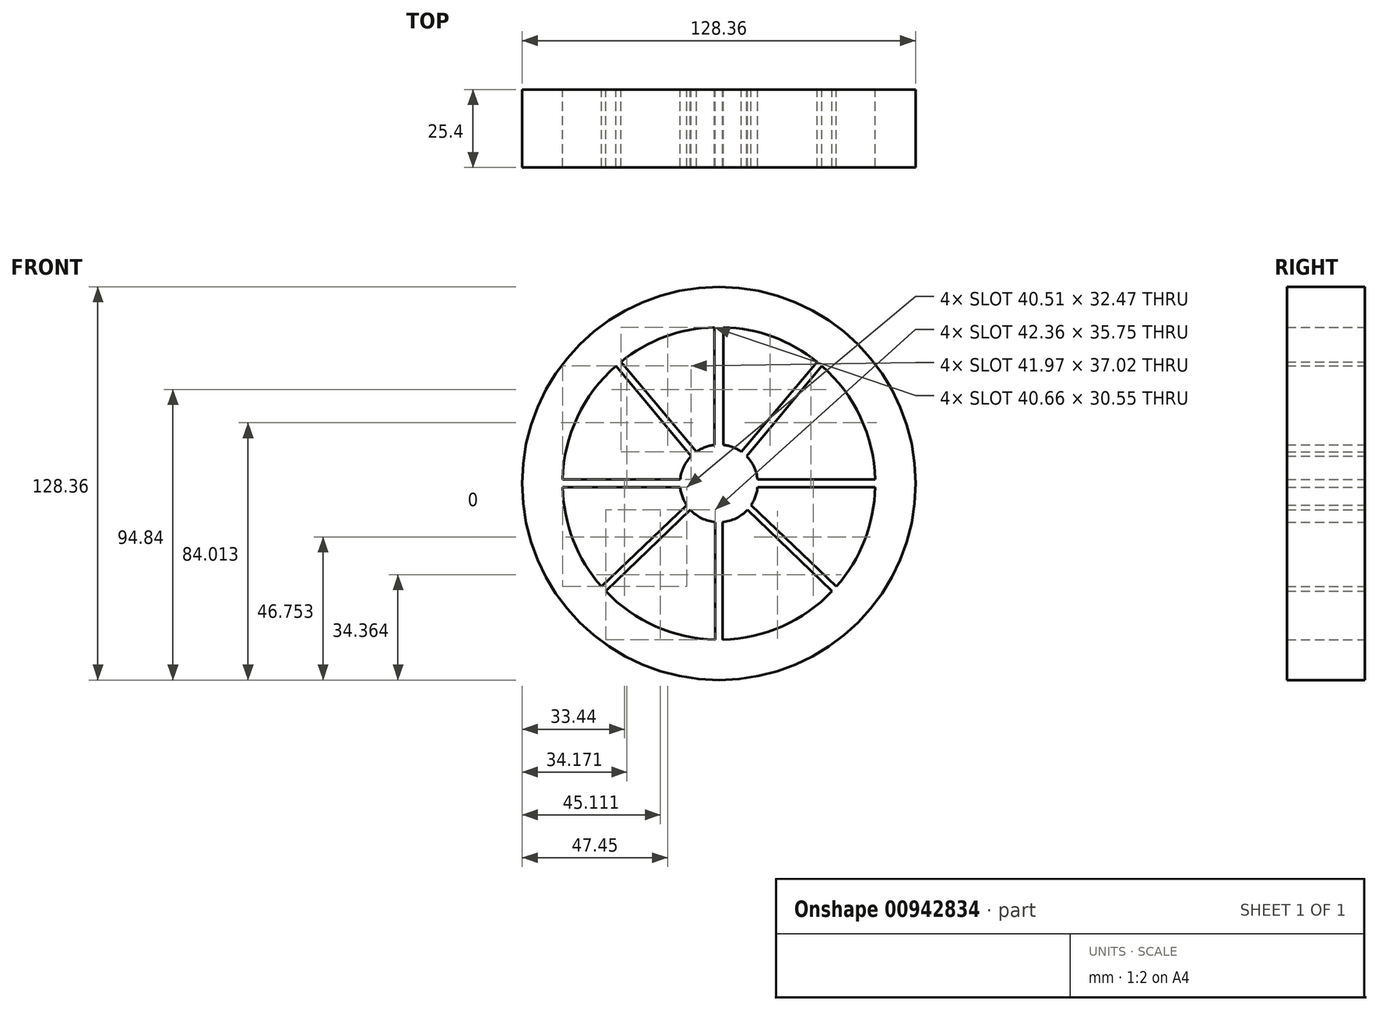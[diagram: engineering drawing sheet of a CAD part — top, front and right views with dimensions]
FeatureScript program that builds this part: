
annotation { "Feature Type Name" : "Feature", "Feature Type Description" : "" }
export const myFeature = defineFeature(function(context is Context, id is Id, definition is map)
    precondition{}
    {
        {
            var Q0;
            Q0=qCreatedBy(makeId("Front.planeOp"),FACE);
            var sketch = newSketch(context, id + "F0", { "sketchPlane" : qUnion([Q0])});
            skCircle(sketch, "E0", {"center": v(0, 0) * mm, "radius": 51 * mm});
            skCircle(sketch, "E1", {"center": v(0, 0) * mm, "radius": 12.67 * mm});
            skLineSegment(sketch, "E2", {"start": v(-1.46, 12.6) * mm, "end": v(-1.46, 50.99) * mm});
            skLineSegment(sketch, "E3", {"start": v(-7.34, 10.33) * mm, "end": v(-32, 39.72) * mm});
            skLineSegment(sketch, "E4", {"start": v(-9.03, 8.9) * mm, "end": v(-33.64, 38.34) * mm});
            skLineSegment(sketch, "E5", {"start": v(-12.6, 1.32) * mm, "end": v(-51, 1.32) * mm});
            skLineSegment(sketch, "E6", {"start": v(-12.62, -1.2) * mm, "end": v(-51, -1.2) * mm});
            skLineSegment(sketch, "E7", {"start": v(-10.49, -7.12) * mm, "end": v(-38.33, -33.66) * mm});
            skLineSegment(sketch, "E8", {"start": v(-9.28, -8.64) * mm, "end": v(-36.94, -35.17) * mm});
            skLineSegment(sketch, "E9", {"start": v(-1.2, -12.62) * mm, "end": v(-1.2, -51) * mm});
            skLineSegment(sketch, "E10.MirrorCS", {"start": v(7.34, 10.33) * mm, "end": v(32, 39.72) * mm});
            skLineSegment(sketch, "E11.MirrorCS", {"start": v(9.03, 8.9) * mm, "end": v(33.64, 38.34) * mm});
            skLineSegment(sketch, "E12.MirrorCS", {"start": v(12.6, 1.32) * mm, "end": v(51, 1.32) * mm});
            skLineSegment(sketch, "E13.MirrorCS", {"start": v(12.62, -1.2) * mm, "end": v(51, -1.2) * mm});
            skLineSegment(sketch, "E14.MirrorCS", {"start": v(10.49, -7.12) * mm, "end": v(38.33, -33.66) * mm});
            skLineSegment(sketch, "E15.MirrorCS", {"start": v(9.28, -8.64) * mm, "end": v(36.94, -35.17) * mm});
            skLineSegment(sketch, "E16.MirrorCS", {"start": v(1.46, 12.6) * mm, "end": v(1.46, 50.99) * mm});
            skLineSegment(sketch, "E17.MirrorCS", {"start": v(1.2, -12.62) * mm, "end": v(1.2, -51) * mm});
            skCircle(sketch, "E18", {"center": v(0, 0) * mm, "radius": 64.18 * mm});
            skSolve(sketch);
        }
        {
            var Q0;
            Q0=makeQuery(id+"F0.imprint","IMPRINT",FACE,{"disambiguationData":[TD([[makeQuery(id+"F0.imprint","IMPRINT",EDGE,{"derivedFrom":sQuery(id+"F0.wireOp",EDGE,"E18")}),1.0]])]});
            var Q1;
            {var subQ0=sQuery(id+"F0.wireOp",EDGE,"E3");Q1=makeQuery(id+"F0.imprint","IMPRINT",FACE,{"disambiguationData":[TD([[makeQuery(id+"F0.imprint","IMPRINT",EDGE,{"derivedFrom":subQ0}),1.0]])]});}
            var Q2;
            {var subQ0=sQuery(id+"F0.wireOp",EDGE,"E2");Q2=makeQuery(id+"F0.imprint","IMPRINT",FACE,{"disambiguationData":[TD([[makeQuery(id+"F0.imprint","IMPRINT",EDGE,{"derivedFrom":subQ0}),-1.0]])]});}
            var Q3;
            {var subQ0=sQuery(id+"F0.wireOp",EDGE,"E10.MirrorCS");Q3=makeQuery(id+"F0.imprint","IMPRINT",FACE,{"disambiguationData":[TD([[makeQuery(id+"F0.imprint","IMPRINT",EDGE,{"derivedFrom":subQ0}),-1.0]])]});}
            var Q4;
            {var subQ0=sQuery(id+"F0.wireOp",EDGE,"E1");var subQ8=makeQuery(id+"F0.imprint","INTERSECT",VERTEX,{"derivedFrom":[subQ0,sQuery(id+"F0.wireOp",EDGE,"E11.MirrorCS")]});Q4=makeQuery(id+"F0.imprint","IMPRINT",FACE,{"disambiguationData":[TD([[makeQuery(id+"F0.imprint","IMPRINT",EDGE,{"disambiguationData":[TD([[subQ8,1.0]])],"derivedFrom":subQ0}),1.0]])]});}
            var Q5;
            {var subQ0=sQuery(id+"F0.wireOp",EDGE,"E12.MirrorCS");Q5=makeQuery(id+"F0.imprint","IMPRINT",FACE,{"disambiguationData":[TD([[makeQuery(id+"F0.imprint","IMPRINT",EDGE,{"derivedFrom":subQ0}),-1.0]])]});}
            var Q6;
            {var subQ0=sQuery(id+"F0.wireOp",EDGE,"E14.MirrorCS");Q6=makeQuery(id+"F0.imprint","IMPRINT",FACE,{"disambiguationData":[TD([[makeQuery(id+"F0.imprint","IMPRINT",EDGE,{"derivedFrom":subQ0}),-1.0]])]});}
            var Q7;
            {var subQ0=sQuery(id+"F0.wireOp",EDGE,"E9");Q7=makeQuery(id+"F0.imprint","IMPRINT",FACE,{"disambiguationData":[TD([[makeQuery(id+"F0.imprint","IMPRINT",EDGE,{"derivedFrom":subQ0}),1.0]])]});}
            var Q8;
            {var subQ0=sQuery(id+"F0.wireOp",EDGE,"E7");Q8=makeQuery(id+"F0.imprint","IMPRINT",FACE,{"disambiguationData":[TD([[makeQuery(id+"F0.imprint","IMPRINT",EDGE,{"derivedFrom":subQ0}),1.0]])]});}
            var Q9;
            {var subQ0=sQuery(id+"F0.wireOp",EDGE,"E5");Q9=makeQuery(id+"F0.imprint","IMPRINT",FACE,{"disambiguationData":[TD([[makeQuery(id+"F0.imprint","IMPRINT",EDGE,{"derivedFrom":subQ0}),1.0]])]});}
            extrude(context, id + "F1", {"entities" : qUnion([Q0, Q1, Q2, Q3, Q4, Q5, Q6, Q7, Q8, Q9]), "depth" : 25.4 * mm, "offsetDistance" : 25.4 * mm});
        }
    });
